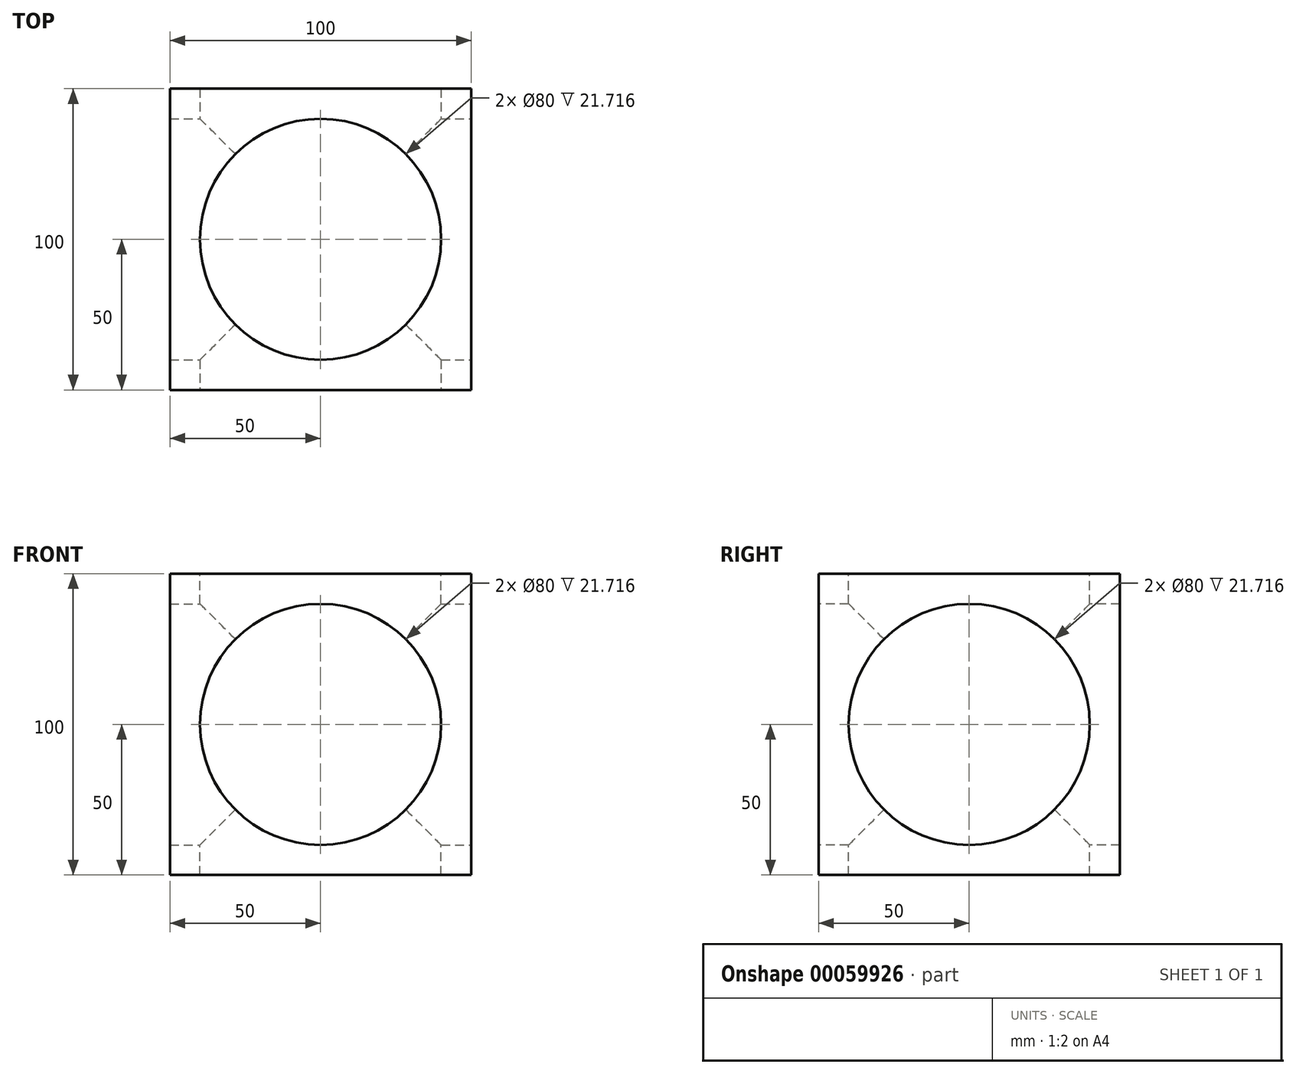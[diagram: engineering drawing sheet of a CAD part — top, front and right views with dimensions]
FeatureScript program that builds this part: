
annotation { "Feature Type Name" : "Feature", "Feature Type Description" : "" }
export const myFeature = defineFeature(function(context is Context, id is Id, definition is map)
    precondition{}
    {
        {
            var Q0;
            Q0=qCreatedBy(makeId("Front.planeOp"),FACE);
            var sketch = newSketch(context, id + "F0", { "sketchPlane" : qUnion([Q0])});
            skLineSegment(sketch, "E0.rect.bottom", {"start": v(50, 50) * mm, "end": v(-50, 50) * mm});
            skLineSegment(sketch, "E0.rect.top", {"start": v(50, -50) * mm, "end": v(-50, -50) * mm});
            skLineSegment(sketch, "E0.rect.left", {"start": v(50, 50) * mm, "end": v(50, -50) * mm});
            skLineSegment(sketch, "E0.rect.right", {"start": v(-50, 50) * mm, "end": v(-50, -50) * mm});
            skPoint(sketch, "E0.rect.middle", {"position": v(0, 0) * mm});
            skSolve(sketch);
        }
        {
            var Q0;
            Q0=makeQuery(id+"F0.imprint","IMPRINT",FACE,{"disambiguationData":[TD([[makeQuery(id+"F0.imprint","IMPRINT",EDGE,{"derivedFrom":sQuery(id+"F0.wireOp",EDGE,"E0.rect.bottom")}),1.0]])]});
            extrude(context, id + "F1", {"entities" : qUnion([Q0]), "endBound" : BoundingType.SYMMETRIC, "depth" : 100 * mm});
        }
        {
            var Q0;
            Q0=makeQuery(id+"F1.opExtrude","CAP_FACE",FACE,{"disambiguationData":[OSD([sQuery(id+"F0.wireOp",EDGE,"E0.rect.bottom"),sQuery(id+"F0.wireOp",EDGE,"E0.rect.top"),sQuery(id+"F0.wireOp",EDGE,"E0.rect.left"),sQuery(id+"F0.wireOp",EDGE,"E0.rect.right")])],"isStart":false});
            var sketch = newSketch(context, id + "F2", { "sketchPlane" : qUnion([Q0])});
            skPoint(sketch, "E1", {"position": v(0, 0) * mm});
            skSolve(sketch);
        }
        {
            var Q0;
            Q0=makeQuery(id+"F1.opExtrude","SWEPT_FACE",FACE,{"disambiguationData":[OSD([sQuery(id+"F0.wireOp",EDGE,"E0.rect.left")])]});
            var sketch = newSketch(context, id + "F3", { "sketchPlane" : qUnion([Q0])});
            skPoint(sketch, "E2", {"position": v(0, 0) * mm});
            skSolve(sketch);
        }
        {
            var Q0;
            Q0=makeQuery(id+"F1.opExtrude","SWEPT_FACE",FACE,{"disambiguationData":[OSD([sQuery(id+"F0.wireOp",EDGE,"E0.rect.bottom")])]});
            var sketch = newSketch(context, id + "F4", { "sketchPlane" : qUnion([Q0])});
            skPoint(sketch, "E3", {"position": v(0, 0) * mm});
            skSolve(sketch);
        }
        {
            var Q0;
            Q0=sQuery(id+"F2.wireOp",VERTEX,"E1");
            var Q1;
            Q1=sQuery(id+"F4.wireOp",VERTEX,"E3");
            var Q2;
            Q2=sQuery(id+"F3.wireOp",VERTEX,"E2");
            var Q3;
            Q3=makeQuery(id+"F1.opExtrude","SWEPT_BODY",BODY,{"disambiguationData":[OSD([sQuery(id+"F0.wireOp",EDGE,"E0.rect.bottom"),sQuery(id+"F0.wireOp",EDGE,"E0.rect.top"),sQuery(id+"F0.wireOp",EDGE,"E0.rect.left"),sQuery(id+"F0.wireOp",EDGE,"E0.rect.right")])]});
            hole(context, id + "F5", {"style" : HoleStyle.SIMPLE, "holeDiameter" : 80 * mm, "endStyle" : HoleEndStyle.THROUGH, "locations" : qUnion([Q0, Q1, Q2]), "scope" : qUnion([Q3])});
        }
    });
